# Revit family: 1Doors_Mincey-Marble-Manufacturing_Madison
name_source: partatom
category: Doors
units: mm (PartAtom-declared; Revit-internal decimal feet)

## family parameters
Always vertical = Yes
Cut with Voids When Loaded = No
OmniClass Number = 23.45.05.14.11.24
Room Calculation Point = No
Shared = No
Work Plane-Based = No

## types (1)
- MADBP - 60 X 78 - Polished - Clear
    Default Elevation = 0"
    Description = Frameless ByPass Barn
    Glass Material = Mincey Marble Manufacturing - Glass - Clear
    Height = 78"
    Height Note = Available custom sizes. Please, contact the manufacturer.
    Manufacturer = Mincey Marble Manufacturing
    Model = MADBP - 60 X 78 - Polished - Clear
    Product Documentation Link = https://minceymarble.com
    Product Material = Mincey Marble Manufacturing - Metal - Polished
    Product Page URL = https://minceymarble.com
    Rough Height = 78"
    Rough Width = 60"
    Thickness = 12 3/4"
    URL = https://minceymarble.com
    Version = 1
    Width = 60"
    Width Note = Available custom sizes. Please, contact the manufacturer.

## geometry (parser evidence)
native form markers: Sweep x3
no freeform markers — native parametric forms only
